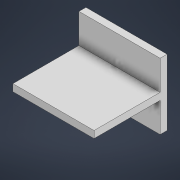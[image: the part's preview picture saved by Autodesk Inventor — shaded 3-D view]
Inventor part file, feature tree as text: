
AUTODESK INVENTOR PART (.ipt)
format: ipt  version: 2022 (Build 260153000, 153)  size: 97,792 bytes
history: native  units: mm
features: extrude x2, sketch x2
ambient origin geometry x8: Origin, YZ Plane, XZ Plane, XY Plane, X Axis, Y Axis, Z Axis, Center Point
bodies: Solid1 (feature_tree)
feature tree (4):
  extrude  "Extrusion1"  Depth=28.5mm
  extrude  "Extrusion2"  Depth=3.0mm
  sketch  "Sketch1"  dims[d0=35.0mm d1=28.5mm]
  sketch  "Sketch2"  dims[d2=3.0mm d3=0.0mm d4=3.0mm d5=28.5mm d6=0.0mm]
